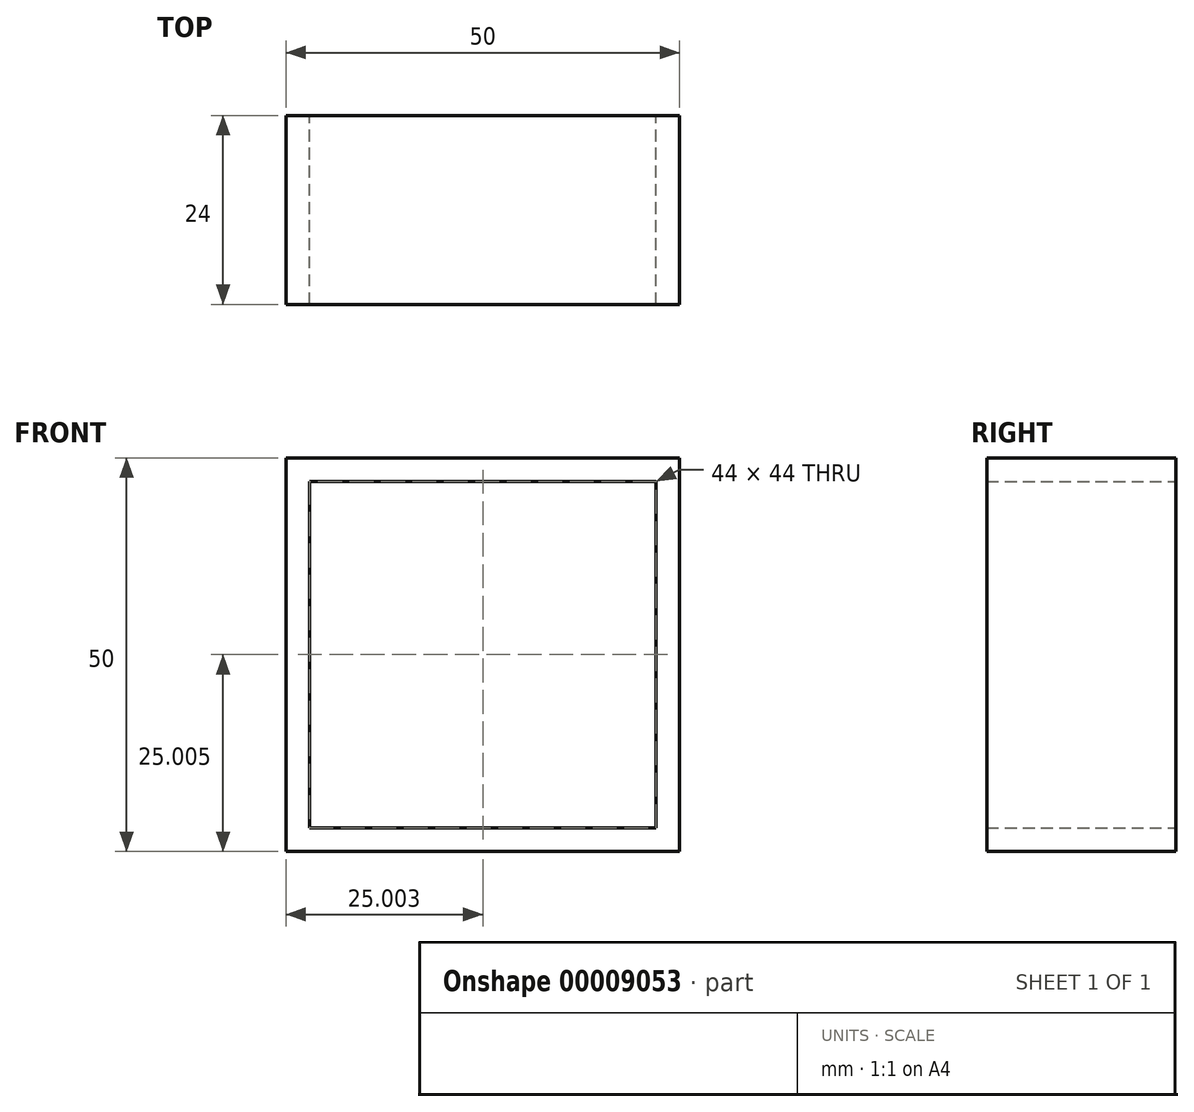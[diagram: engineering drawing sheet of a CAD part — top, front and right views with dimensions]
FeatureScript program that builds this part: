
annotation { "Feature Type Name" : "Feature", "Feature Type Description" : "" }
export const myFeature = defineFeature(function(context is Context, id is Id, definition is map)
    precondition{}
    {
        {
            var Q0;
            Q0=qCreatedBy(makeId("Front.planeOp"),FACE);
            var sketch = newSketch(context, id + "F0", { "sketchPlane" : qUnion([Q0])});
            skLineSegment(sketch, "E0.bottom", {"start": v(-20.92, 25.5) * mm, "end": v(29.08, 25.5) * mm});
            skLineSegment(sketch, "E0.top", {"start": v(-20.92, -24.5) * mm, "end": v(29.08, -24.5) * mm});
            skLineSegment(sketch, "E0.left", {"start": v(-20.92, 25.5) * mm, "end": v(-20.92, -24.5) * mm});
            skLineSegment(sketch, "E0.right", {"start": v(29.08, 25.5) * mm, "end": v(29.08, -24.5) * mm});
            skLineSegment(sketch, "E1.bottom", {"start": v(-17.92, 22.5) * mm, "end": v(26.08, 22.5) * mm});
            skLineSegment(sketch, "E1.top", {"start": v(-17.92, -21.5) * mm, "end": v(26.08, -21.5) * mm});
            skLineSegment(sketch, "E1.left", {"start": v(-17.92, 22.5) * mm, "end": v(-17.92, -21.5) * mm});
            skLineSegment(sketch, "E1.right", {"start": v(26.08, 22.5) * mm, "end": v(26.08, -21.5) * mm});
            skSolve(sketch);
        }
        {
            var Q0;
            Q0 = qSketchRegion(id + "F0", true);
            extrude(context, id + "F1", {"entities" : qUnion([Q0]), "depth" : 24 * mm});
        }
    });
